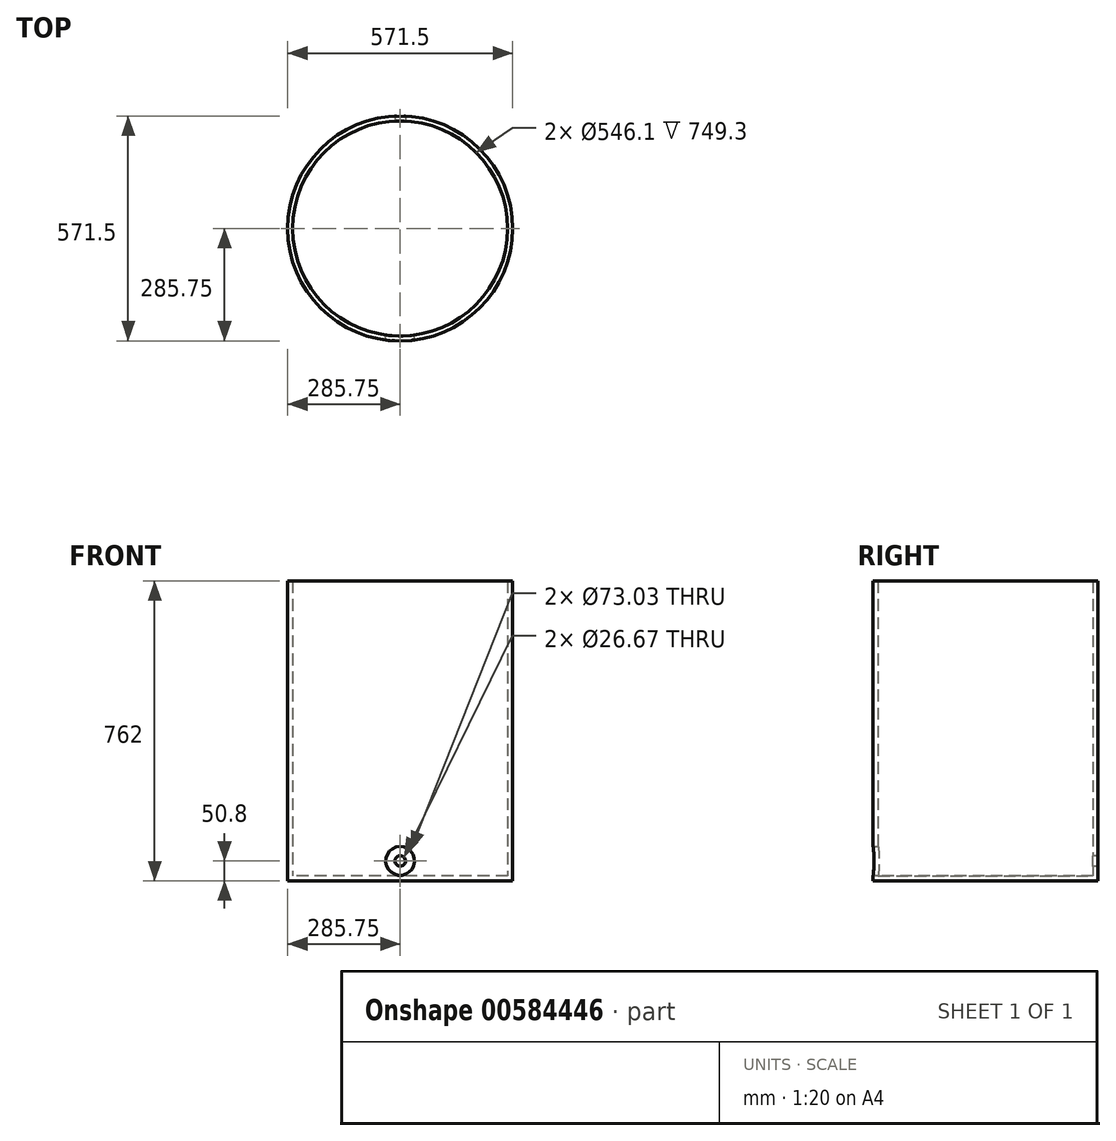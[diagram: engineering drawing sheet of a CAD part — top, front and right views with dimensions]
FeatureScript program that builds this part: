
annotation { "Feature Type Name" : "Feature", "Feature Type Description" : "" }
export const myFeature = defineFeature(function(context is Context, id is Id, definition is map)
    precondition{}
    {
        {
            var Q0;
            Q0=qCreatedBy(makeId("Top.planeOp"),FACE);
            var sketch = newSketch(context, id + "F0", { "sketchPlane" : qUnion([Q0])});
            skCircle(sketch, "E0", {"center": v(0, 0) * mm, "radius": 285.75 * mm});
            skSolve(sketch);
        }
        {
            var Q0;
            Q0=qSketchRegion(id+"F0",true);
            extrude(context, id + "F1", {"entities" : qUnion([Q0]), "depth" : 762 * mm, "offsetDistance" : 25.4 * mm});
        }
        {
            var Q0;
            Q0=makeQuery(id+"F1.opExtrude","CAP_FACE",FACE,{"disambiguationData":[OSD([sQuery(id+"F0.wireOp",EDGE,"E0")])],"isStart":false});
            shell(context, id + "F2", {"entities" : qUnion([Q0]), "thickness" : 12.7 * mm});
        }
        {
            var Q0;
            Q0=qCreatedBy(makeId("Front.planeOp"),FACE);
            var sketch = newSketch(context, id + "F3", { "sketchPlane" : qUnion([Q0])});
            skLineSegment(sketch, "E1", {"start": v(0, 0) * mm, "end": v(0, 101.6) * mm, "construction": true});
            skCircle(sketch, "E2", {"center": v(0, 50.8) * mm, "radius": 36.51 * mm});
            skSolve(sketch);
        }
        {
            var Q0;
            Q0=qSketchRegion(id+"F3",true);
            extrude(context, id + "F4", {"entities" : qUnion([Q0]), "operationType" : NewBodyOperationType.REMOVE, "depth" : 327.66 * mm, "offsetDistance" : 25.4 * mm});
        }
        {
            var Q0;
            Q0=qCreatedBy(makeId("Front.planeOp"),FACE);
            var sketch = newSketch(context, id + "F5", { "sketchPlane" : qUnion([Q0])});
            skLineSegment(sketch, "E3", {"start": v(0, 0) * mm, "end": v(0, 101.6) * mm, "construction": true});
            skCircle(sketch, "E4", {"center": v(0, 50.8) * mm, "radius": 13.34 * mm});
            skSolve(sketch);
        }
        {
            var Q0;
            Q0 = qSketchRegion(id + "F5", true);
            extrude(context, id + "F6", {"entities" : qUnion([Q0]), "operationType" : NewBodyOperationType.REMOVE, "oppositeDirection" : true, "depth" : 345.44 * mm, "offsetDistance" : 25.4 * mm});
        }
    });
